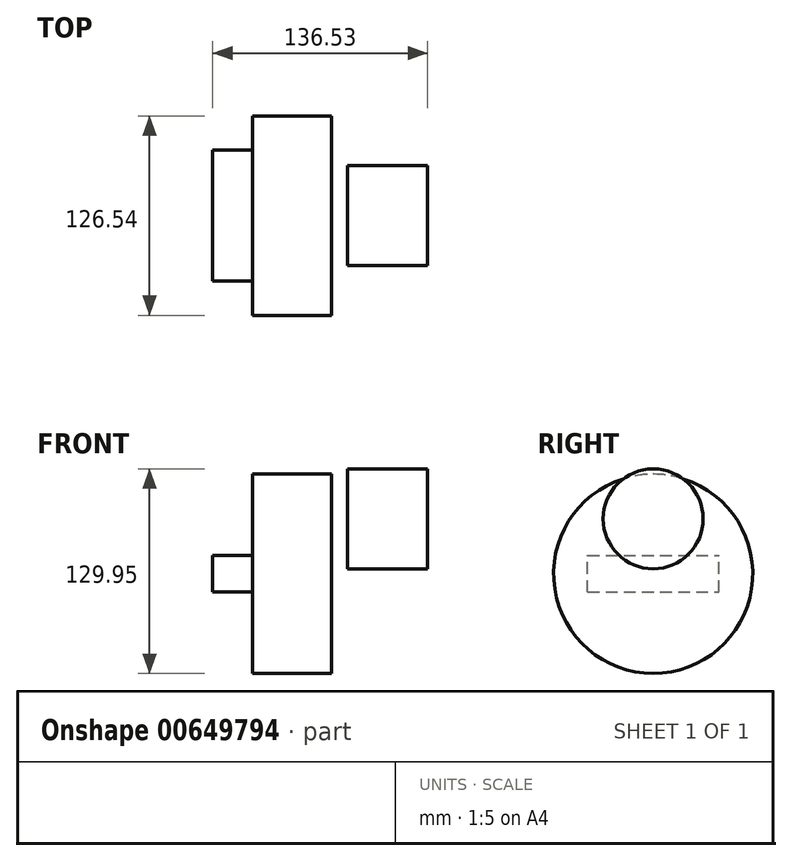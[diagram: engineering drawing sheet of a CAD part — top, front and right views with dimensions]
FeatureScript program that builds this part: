
annotation { "Feature Type Name" : "Feature", "Feature Type Description" : "" }
export const myFeature = defineFeature(function(context is Context, id is Id, definition is map)
    precondition{}
    {
        {
            var Q0;
            Q0=qCreatedBy(makeId("Front.planeOp"),FACE);
            var sketch = newSketch(context, id + "F0", { "sketchPlane" : qUnion([Q0])});
            skLineSegment(sketch, "E0.bottom", {"start": v(41.27, 9.53) * mm, "end": v(-41.27, 9.53) * mm});
            skLineSegment(sketch, "E0.top", {"start": v(41.28, -9.52) * mm, "end": v(-41.27, -9.52) * mm});
            skLineSegment(sketch, "E0.left", {"start": v(41.27, 9.53) * mm, "end": v(41.28, -9.52) * mm});
            skLineSegment(sketch, "E0.right", {"start": v(-41.27, 9.53) * mm, "end": v(-41.27, -9.52) * mm});
            skPoint(sketch, "E0.middle", {"position": v(0, 0) * mm});
            skLineSegment(sketch, "E1", {"start": v(41.27, 9.53) * mm, "end": v(41.27, 34.93) * mm});
            skArc(sketch, "E2", {"start": v(47.62, 41.28) * mm, "mid": v(43.13, 39.42) * mm, "end": v(41.27, 34.93) * mm});
            skLineSegment(sketch, "E3", {"start": v(47.62, 41.28) * mm, "end": v(73.02, 41.28) * mm});
            skLineSegment(sketch, "E4.0", {"start": v(47.62, 60.33) * mm, "end": v(73.02, 60.33) * mm});
            skArc(sketch, "E4.1", {"start": v(47.62, 60.33) * mm, "mid": v(29.66, 52.89) * mm, "end": v(22.22, 34.93) * mm});
            skLineSegment(sketch, "E4.2", {"start": v(22.22, 9.53) * mm, "end": v(22.22, 34.93) * mm});
            skLineSegment(sketch, "E5.bottom", {"start": v(111.12, 34.93) * mm, "end": v(60.32, 34.93) * mm});
            skLineSegment(sketch, "E5.top", {"start": v(111.12, 66.68) * mm, "end": v(60.32, 66.68) * mm});
            skLineSegment(sketch, "E5.left", {"start": v(111.12, 34.93) * mm, "end": v(111.12, 66.68) * mm});
            skLineSegment(sketch, "E5.right", {"start": v(60.32, 34.93) * mm, "end": v(60.32, 66.68) * mm});
            skPoint(sketch, "E5.middle", {"position": v(85.72, 50.8) * mm});
            skSolve(sketch);
        }
        {
            var Q0;
            {var subQ1=sQuery(id+"F0.wireOp",EDGE,"E5.bottom");Q0=makeQuery(id+"F0.imprint","IMPRINT",FACE,{"disambiguationData":[TD([[makeQuery(id+"F0.imprint","IMPRINT",EDGE,{"derivedFrom":subQ1}),-1.0]])]});}
            var Q1;
            Q1=sQuery(id+"F0.wireOp",EDGE,"E5.bottom");
            revolve(context, id + "F1", {"entities" : qUnion([Q0]), "axis" : qUnion([Q1]), "revolveType" : RevolveType.FULL});
        }
        {
            var Q0;
            Q0=qCreatedBy(makeId("Front.planeOp"),FACE);
            var sketch = newSketch(context, id + "F2", { "sketchPlane" : qUnion([Q0])});
            skLineSegment(sketch, "E6", {"start": v(0, 0) * mm, "end": v(0, -63.27) * mm});
            skLineSegment(sketch, "E7", {"start": v(0, -63.27) * mm, "end": v(49.97, -63.27) * mm});
            skLineSegment(sketch, "E8", {"start": v(49.97, -63.27) * mm, "end": v(49.97, 0) * mm});
            skLineSegment(sketch, "E9", {"start": v(49.97, 0) * mm, "end": v(0, 0) * mm});
            skSolve(sketch);
        }
        {
            var Q0;
            Q0=makeQuery(id+"F2.imprint","IMPRINT",FACE,{"disambiguationData":[TD([[makeQuery(id+"F2.imprint","IMPRINT",EDGE,{"derivedFrom":sQuery(id+"F2.wireOp",EDGE,"E6")}),1.0]])]});
            var Q1;
            Q1=sQuery(id+"F2.wireOp",EDGE,"E9");
            revolve(context, id + "F3", {"entities" : qUnion([Q0]), "axis" : qUnion([Q1]), "revolveType" : RevolveType.FULL});
        }
        {
            var Q0;
            Q0=makeQuery(id+"F3.opRevolve","SWEPT_FACE",FACE,{"disambiguationData":[OSD([sQuery(id+"F2.wireOp",EDGE,"E6")])]});
            var sketch = newSketch(context, id + "F4", { "sketchPlane" : qUnion([Q0])});
            skCircle(sketch, "E10", {"center": v(0, 0) * mm, "radius": 41.48 * mm});
            skSolve(sketch);
        }
        {
            var Q0;
            Q0=makeQuery(id+"F4.imprint","IMPRINT",FACE,{"disambiguationData":[TD([[makeQuery(id+"F4.imprint","IMPRINT",EDGE,{"derivedFrom":sQuery(id+"F4.wireOp",EDGE,"E10")}),1.0]])]});
            var Q1;
            Q1=makeQuery(id+"F3.opRevolve","SWEPT_FACE",FACE,{"disambiguationData":[OSD([sQuery(id+"F2.wireOp",EDGE,"E8")])]});
            extrude(context, id + "F5", {"entities" : qUnion([Q0]), "operationType" : NewBodyOperationType.ADD, "endBound" : BoundingType.UP_TO_SURFACE, "oppositeDirection" : true, "depth" : 110.97 * mm, "endBoundEntityFace" : qUnion([Q1]), "offsetDistance" : 25.4 * mm});
        }
        {
            var Q0;
            Q0=makeQuery(id+"F3.opRevolve","SWEPT_FACE",FACE,{"disambiguationData":[OSD([sQuery(id+"F2.wireOp",EDGE,"E6")])]});
            var sketch = newSketch(context, id + "F6", { "sketchPlane" : qUnion([Q0])});
            skLineSegment(sketch, "E11.bottom", {"start": v(41.6, -11.62) * mm, "end": v(-41.6, -11.62) * mm});
            skLineSegment(sketch, "E11.top", {"start": v(41.6, 11.62) * mm, "end": v(-41.6, 11.62) * mm});
            skLineSegment(sketch, "E11.left", {"start": v(41.6, -11.62) * mm, "end": v(41.6, 11.62) * mm});
            skLineSegment(sketch, "E11.right", {"start": v(-41.6, -11.62) * mm, "end": v(-41.6, 11.62) * mm});
            skPoint(sketch, "E11.middle", {"position": v(0, 0) * mm});
            skSolve(sketch);
        }
        {
            var Q0;
            Q0 = qSketchRegion(id + "F6", true);
            extrude(context, id + "F7", {"entities" : qUnion([Q0]), "operationType" : NewBodyOperationType.ADD, "depth" : 25.4 * mm, "offsetDistance" : 25.4 * mm});
        }
    });
